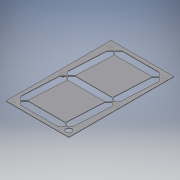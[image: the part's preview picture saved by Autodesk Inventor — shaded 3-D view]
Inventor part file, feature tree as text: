
AUTODESK INVENTOR PART (.ipt)
format: ipt  version: 2016 SP2 (Build 200236200, 236)  size: 185,344 bytes
history: native  units: mm
features: reference x5, extrude x2, sketch x2
ambient origin geometry x8: Origin, YZ Plane, XZ Plane, XY Plane, X Axis, Y Axis, Z Axis, Center Point
bodies: Volumenkörper1 (feature_tree)
feature tree (9):
  extrude  "Extrusion1"  Depth=8.0mm
  extrude  "Extrusion2"  Depth=5.0mm
  sketch  "Skizze1"  dims[d24=8.0mm d25=8.0mm]
  sketch  "Skizze3"  dims[d26=8.0mm d27=5.0mm d28=10.0mm d30=1.0mm d31=0.523599mm d32=0.0mm d33=10.0mm d34=135.0deg d35=1.0mm d36=0.0mm d37=1.0mm d38=0.0mm d39=1.0mm d40=0.0mm d41=1.0mm d42=5.0mm d43=10.0mm d44=1.0mm d45=1.0mm d46=0.6mm d47=0.0mm d48=50.0mm d49=85.233596mm d50=142.691381mm d51=4.8mm d52=4.8mm d53=4.8mm d54=4.8mm d55=4.8mm d56=2.5mm d57=0.0mm]
  reference  "Referenz1"
  reference  "Referenz2"
  reference  "Referenz3"
  reference  "Referenz4"
  reference  "Referenz5"
